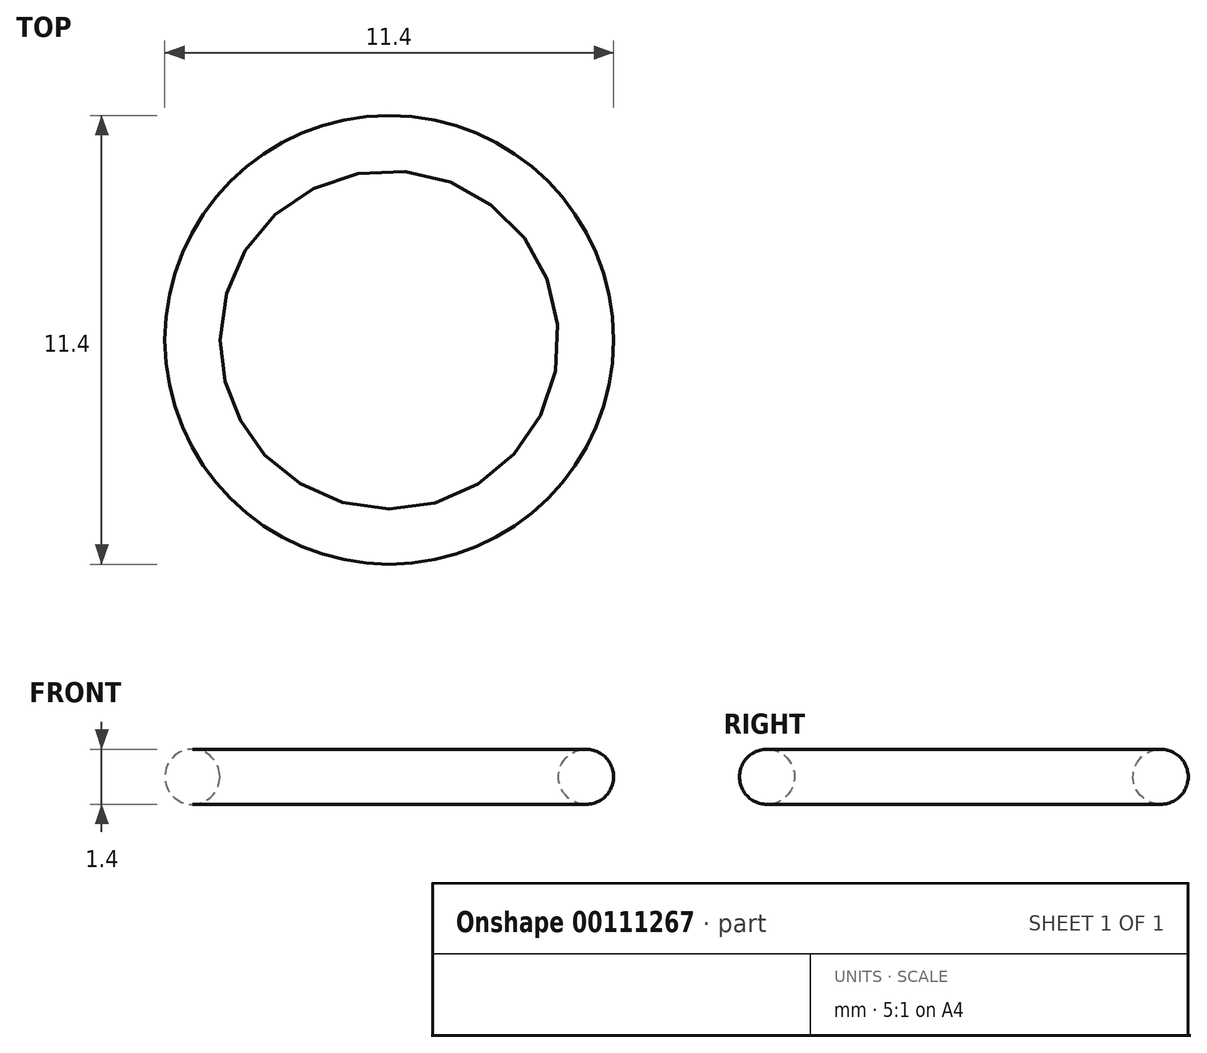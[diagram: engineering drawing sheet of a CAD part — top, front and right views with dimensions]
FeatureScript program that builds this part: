
annotation { "Feature Type Name" : "Feature", "Feature Type Description" : "" }
export const myFeature = defineFeature(function(context is Context, id is Id, definition is map)
    precondition{}
    {
        {
            var Q0;
            Q0=qCreatedBy(makeId("Top.planeOp"),FACE);
            var sketch = newSketch(context, id + "F0", { "sketchPlane" : qUnion([Q0])});
            skCircle(sketch, "E0", {"center": v(0, 0) * mm, "radius": 5 * mm, "construction": true});
            skSolve(sketch);
        }
        {
            var Q0;
            Q0=qCreatedBy(makeId("Right.planeOp"),FACE);
            var sketch = newSketch(context, id + "F1", { "sketchPlane" : qUnion([Q0])});
            skLineSegment(sketch, "E1.0", {"start": v(-5, 0) * mm, "end": v(5, 0) * mm, "construction": true});
            skCircle(sketch, "E2", {"center": v(5, 0) * mm, "radius": 0.7 * mm});
            skLineSegment(sketch, "E3", {"start": v(0, 0) * mm, "end": v(0, 16.14) * mm, "construction": true});
            skSolve(sketch);
        }
        {
            var Q0;
            Q0=makeQuery(id+"F1.imprint","IMPRINT",FACE,{"disambiguationData":[TD([[makeQuery(id+"F1.imprint","IMPRINT",EDGE,{"derivedFrom":sQuery(id+"F1.wireOp",EDGE,"E2")}),1.0]])]});
            var Q1;
            Q1=sQuery(id+"F1.wireOp",EDGE,"E3");
            revolve(context, id + "F2", {"entities" : qUnion([Q0]), "axis" : qUnion([Q1]), "revolveType" : RevolveType.FULL});
        }
    });
